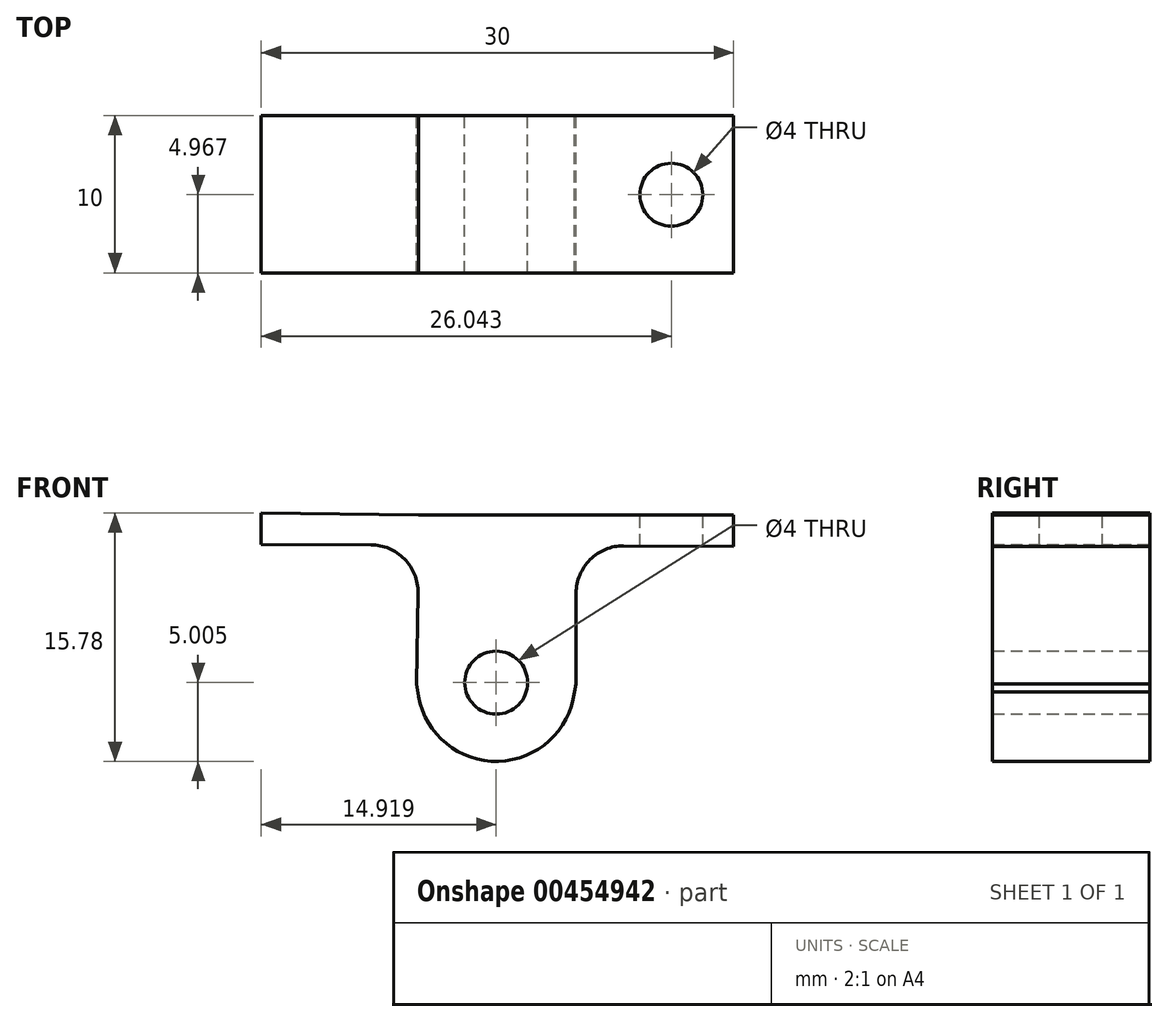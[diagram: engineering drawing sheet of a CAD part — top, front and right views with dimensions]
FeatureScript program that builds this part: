
annotation { "Feature Type Name" : "Feature", "Feature Type Description" : "" }
export const myFeature = defineFeature(function(context is Context, id is Id, definition is map)
    precondition{}
    {
        {
            var Q0;
            Q0=qCreatedBy(makeId("Front.planeOp"),FACE);
            var sketch = newSketch(context, id + "F0", { "sketchPlane" : qUnion([Q0])});
            skLineSegment(sketch, "E0.bottom", {"start": v(-23.38, 34.6) * mm, "end": v(-13.38, 34.48) * mm});
            skLineSegment(sketch, "E0.left", {"start": v(-23.38, 34.6) * mm, "end": v(-23.38, 32.6) * mm});
            skLineSegment(sketch, "E1", {"start": v(-23.38, 32.6) * mm, "end": v(-21.3, 32.6) * mm});
            skLineSegment(sketch, "E2", {"start": v(-13.38, 34.48) * mm, "end": v(-3.38, 34.48) * mm});
            skLineSegment(sketch, "E3", {"start": v(-3.38, 34.48) * mm, "end": v(6.62, 34.48) * mm});
            skLineSegment(sketch, "E4", {"start": v(6.62, 34.48) * mm, "end": v(6.62, 32.48) * mm});
            skLineSegment(sketch, "E5", {"start": v(-13.72, 24.48) * mm, "end": v(-13.72, 24.6) * mm});
            skLineSegment(sketch, "E6.filletArc", {"start": v(-13.72, 24.6) * mm, "end": v(-13.72, 24.6) * mm});
            skPoint(sketch, "E7.visualSharp", {"position": v(-18.38, 32.6) * mm});
            skLineSegment(sketch, "E8", {"start": v(-20.71, 32.6) * mm, "end": v(-21.3, 32.6) * mm});
            skLineSegment(sketch, "E9", {"start": v(-0.37, 32.5) * mm, "end": v(6.62, 32.48) * mm});
            skLineSegment(sketch, "E10", {"start": v(-23.38, 32.6) * mm, "end": v(-16.42, 32.57) * mm});
            skPoint(sketch, "E11.visualSharp", {"position": v(-3.38, 32.52) * mm});
            skLineSegment(sketch, "E12", {"start": v(-3.38, 29.5) * mm, "end": v(-3.38, 23.73) * mm});
            skLineSegment(sketch, "E13", {"start": v(-13.43, 29.52) * mm, "end": v(-13.52, 23.73) * mm});
            skPoint(sketch, "E13.endSnap0", {"position": v(-13.52, 28.15) * mm});
            skArc(sketch, "E14", {"start": v(-13.38, 22.94) * mm, "mid": v(-8.32, 18.82) * mm, "end": v(-3.5, 23.21) * mm});
            skPoint(sketch, "E15.visualSharp", {"position": v(-13.38, 32.56) * mm});
            skArc(sketch, "E15.filletArc", {"start": v(-13.43, 29.52) * mm, "mid": v(-14.29, 31.67) * mm, "end": v(-16.42, 32.57) * mm});
            skArc(sketch, "E16.filletArc", {"start": v(-0.37, 32.5) * mm, "mid": v(-2.5, 31.63) * mm, "end": v(-3.38, 29.5) * mm});
            skCircle(sketch, "E17", {"center": v(-8.46, 23.81) * mm, "radius": 2 * mm});
            skLineSegment(sketch, "E18", {"start": v(-3.38, 23.73) * mm, "end": v(-3.5, 23.21) * mm});
            skLineSegment(sketch, "E19", {"start": v(-13.52, 23.73) * mm, "end": v(-13.38, 22.94) * mm});
            skSolve(sketch);
        }
        {
            var Q0;
            Q0=makeQuery(id+"F0.imprint","IMPRINT",FACE,{"disambiguationData":[TD([[makeQuery(id+"F0.imprint","IMPRINT",EDGE,{"derivedFrom":sQuery(id+"F0.wireOp",EDGE,"E0.bottom")}),-1.0]])]});
            extrude(context, id + "F1", {"entities" : qUnion([Q0]), "depth" : 10 * mm, "offsetDistance" : 25 * mm});
        }
        {
            var Q0;
            Q0=makeQuery(id+"F1.opExtrude","SWEPT_FACE",FACE,{"disambiguationData":[OSD([sQuery(id+"F0.wireOp",EDGE,"E0.bottom"),sQuery(id+"F0.wireOp",EDGE,"SCYOV1aV-iGLg-zfcZ-rWRa-Nb9pHx2vml7F"),sQuery(id+"F0.wireOp",EDGE,"E2")])]});
            var sketch = newSketch(context, id + "F2", { "sketchPlane" : qUnion([Q0])});
            skLineSegment(sketch, "E20", {"start": v(-23.78, -5) * mm, "end": v(6.05, -5) * mm});
            skPoint(sketch, "E20.endSnap0", {"position": v(-13.78, -5) * mm});
            skLineSegment(sketch, "E21", {"start": v(-23.78, -5) * mm, "end": v(-19.78, -5) * mm});
            skLineSegment(sketch, "E22", {"start": v(-19.78, -5) * mm, "end": v(2.22, -5) * mm});
            skCircle(sketch, "E23", {"center": v(2.22, -5) * mm, "radius": 2 * mm});
            skCircle(sketch, "E24", {"center": v(-19.78, -5) * mm, "radius": 2 * mm});
            skSolve(sketch);
        }
        {
            var Q0;
            Q0=makeQuery(id+"F1.opExtrude","SWEPT_FACE",FACE,{"disambiguationData":[OSD([sQuery(id+"F0.wireOp",EDGE,"E2"),sQuery(id+"F0.wireOp",EDGE,"E3")])]});
            var sketch = newSketch(context, id + "F3", { "sketchPlane" : qUnion([Q0])});
            skSolve(sketch);
        }
        {
            var Q0;
            {var subQ0=sQuery(id+"F0.wireOp",EDGE,"E2");Q0=makeQuery(id+"F3.imprint","IMPRINT",FACE,{"disambiguationData":[TD([[makeQuery(id+"F3.imprint","IMPRINT",EDGE,{"derivedFrom":makeQuery(id+"F1.opExtrude","SWEPT_EDGE",EDGE,{"disambiguationData":[OSD([sQuery(id+"F0.wireOp",EDGE,"E0.bottom"),subQ0])]})}),-1.0]])]});}
            var sketch = newSketch(context, id + "F4", { "sketchPlane" : qUnion([Q0])});
            skCircle(sketch, "E25", {"center": v(2.66, -5.03) * mm, "radius": 2 * mm});
            skSolve(sketch);
        }
        {
            var Q0;
            Q0=makeQuery(id+"F4.imprint","IMPRINT",FACE,{"disambiguationData":[TD([[makeQuery(id+"F4.imprint","IMPRINT",EDGE,{"derivedFrom":sQuery(id+"F4.wireOp",EDGE,"E25")}),1.0]])]});
            var Q1;
            {var subQ0=sQuery(id+"F2.wireOp",EDGE,"E22");var subQ1=sQuery(id+"F2.wireOp",EDGE,"E21");var subQ2=makeQuery(id+"F2.imprint","INTERSECT",VERTEX,{"derivedFrom":[subQ1,subQ0]});Q1=makeQuery(id+"F2.imprint","IMPRINT",FACE,{"disambiguationData":[TD([[makeQuery(id+"F2.imprint","IMPRINT",EDGE,{"disambiguationData":[TD([[subQ2,1.0]])],"derivedFrom":subQ1}),1.0]])]});}
            var Q2;
            {var subQ0=sQuery(id+"F2.wireOp",EDGE,"E22");var subQ1=sQuery(id+"F2.wireOp",EDGE,"E21");var subQ2=makeQuery(id+"F2.imprint","INTERSECT",VERTEX,{"derivedFrom":[subQ1,subQ0]});Q2=makeQuery(id+"F2.imprint","IMPRINT",FACE,{"disambiguationData":[TD([[makeQuery(id+"F2.imprint","IMPRINT",EDGE,{"disambiguationData":[TD([[subQ2,1.0]])],"derivedFrom":subQ1}),-1.0]])]});}
            var Q3;
            Q3=sQuery(id+"F4.wireOp",EDGE,"E25");
            extrude(context, id + "F5", {"entities" : qUnion([Q0, Q1, Q2]), "operationType" : NewBodyOperationType.REMOVE, "surfaceEntities" : qUnion([Q3]), "oppositeDirection" : true, "depth" : 25 * mm, "offsetDistance" : 25 * mm});
        }
    });
